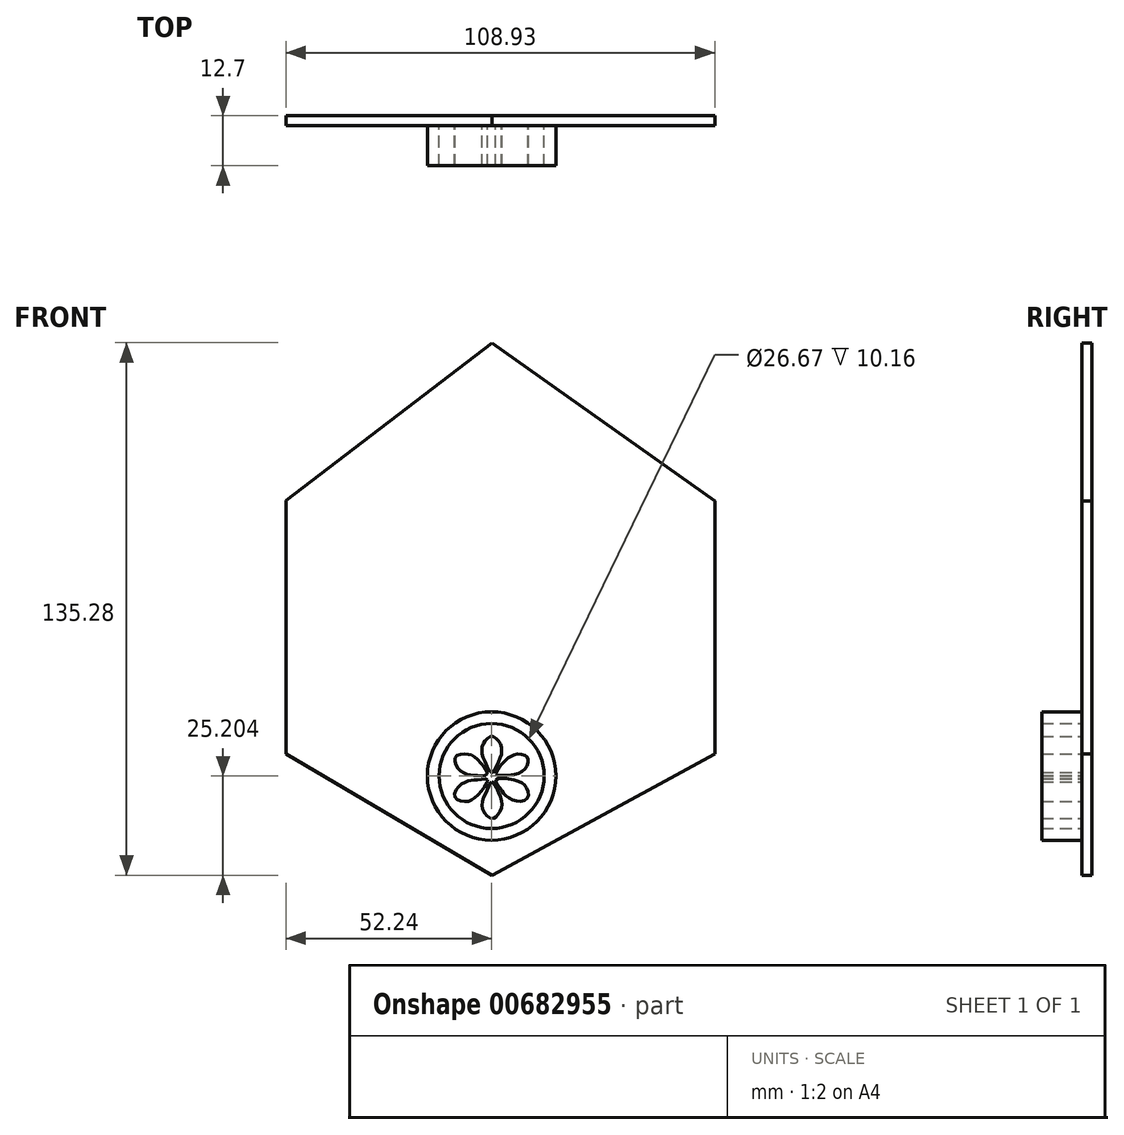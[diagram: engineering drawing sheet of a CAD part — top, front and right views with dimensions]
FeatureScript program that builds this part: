
annotation { "Feature Type Name" : "Feature", "Feature Type Description" : "" }
export const myFeature = defineFeature(function(context is Context, id is Id, definition is map)
    precondition{}
    {
        {
            var Q0;
            Q0=qCreatedBy(makeId("Front.planeOp"),FACE);
            var sketch = newSketch(context, id + "F0", { "sketchPlane" : qUnion([Q0])});
            skLineSegment(sketch, "E0", {"start": v(0, 68.56) * mm, "end": v(59.23, 26.56) * mm});
            skLineSegment(sketch, "E1", {"start": v(59.23, 26.56) * mm, "end": v(59.23, -40.56) * mm});
            skLineSegment(sketch, "E2", {"start": v(59.23, -40.56) * mm, "end": v(0, -72.79) * mm});
            skLineSegment(sketch, "E3", {"start": v(0, -72.79) * mm, "end": v(-54.78, -40.56) * mm});
            skLineSegment(sketch, "E4", {"start": v(-54.78, -40.56) * mm, "end": v(-54.78, 26.56) * mm});
            skLineSegment(sketch, "E5", {"start": v(-54.78, 26.56) * mm, "end": v(0, 68.56) * mm});
            skSolve(sketch);
        }
        {
            var Q0;
            Q0=makeQuery(id+"F0.imprint","IMPRINT",FACE,{"disambiguationData":[TD([[makeQuery(id+"F0.imprint","IMPRINT",EDGE,{"derivedFrom":sQuery(id+"F0.wireOp",EDGE,"E0")}),-1.0]])]});
            extrude(context, id + "F1", {"entities" : qUnion([Q0]), "depth" : 12.7 * mm, "offsetDistance" : 25.4 * mm});
        }
        {
            var Q0;
            Q0=makeQuery(id+"F1.opExtrude","CAP_FACE",FACE,{"disambiguationData":[OSD([sQuery(id+"F0.wireOp",EDGE,"E0"),sQuery(id+"F0.wireOp",EDGE,"E1"),sQuery(id+"F0.wireOp",EDGE,"E2"),sQuery(id+"F0.wireOp",EDGE,"E3"),sQuery(id+"F0.wireOp",EDGE,"E4"),sQuery(id+"F0.wireOp",EDGE,"E5")])],"isStart":false});
            extrude(context, id + "F2", {"entities" : qUnion([Q0]), "operationType" : NewBodyOperationType.REMOVE, "oppositeDirection" : true, "depth" : 2.54 * mm, "offsetDistance" : 25.4 * mm});
        }
        {
            var Q0;
            Q0=makeQuery(id+"F2.boolean.opBoolean","COPY",FACE,{"derivedFrom":makeQuery(id+"F2.opExtrude","CAP_FACE",FACE,{"disambiguationData":[OSD([sQuery(id+"F0.wireOp",EDGE,"E0"),sQuery(id+"F0.wireOp",EDGE,"E1"),sQuery(id+"F0.wireOp",EDGE,"E2"),sQuery(id+"F0.wireOp",EDGE,"E3"),sQuery(id+"F0.wireOp",EDGE,"E4"),sQuery(id+"F0.wireOp",EDGE,"E5")])],"isStart":false})});
            extrude(context, id + "F3", {"entities" : qUnion([Q0]), "operationType" : NewBodyOperationType.REMOVE, "oppositeDirection" : true, "depth" : 7.62 * mm, "offsetDistance" : 25.4 * mm});
        }
        {
            var Q0;
            Q0=makeQuery(id+"F1.opExtrude","SWEPT_FACE",FACE,{"disambiguationData":[OSD([sQuery(id+"F0.wireOp",EDGE,"E0")])]});
            extrude(context, id + "F4", {"entities" : qUnion([Q0]), "operationType" : NewBodyOperationType.REMOVE, "oppositeDirection" : true, "depth" : 2.54 * mm, "offsetDistance" : 25.4 * mm});
        }
        {
            var Q0;
            Q0=makeQuery(id+"F1.opExtrude","SWEPT_FACE",FACE,{"disambiguationData":[OSD([sQuery(id+"F0.wireOp",EDGE,"E5")])]});
            extrude(context, id + "F5", {"entities" : qUnion([Q0]), "operationType" : NewBodyOperationType.REMOVE, "oppositeDirection" : true, "depth" : 2.54 * mm, "offsetDistance" : 25.4 * mm});
        }
        {
            var Q0;
            Q0=makeQuery(id+"F1.opExtrude","SWEPT_FACE",FACE,{"disambiguationData":[OSD([sQuery(id+"F0.wireOp",EDGE,"E1")])]});
            extrude(context, id + "F6", {"entities" : qUnion([Q0]), "operationType" : NewBodyOperationType.REMOVE, "oppositeDirection" : true, "depth" : 2.54 * mm, "offsetDistance" : 25.4 * mm});
        }
        {
            var Q0;
            Q0=makeQuery(id+"F1.opExtrude","SWEPT_FACE",FACE,{"disambiguationData":[OSD([sQuery(id+"F0.wireOp",EDGE,"E4")])]});
            extrude(context, id + "F7", {"entities" : qUnion([Q0]), "operationType" : NewBodyOperationType.REMOVE, "oppositeDirection" : true, "depth" : 2.54 * mm, "offsetDistance" : 25.4 * mm});
        }
        {
            var Q0;
            Q0=makeQuery(id+"F1.opExtrude","SWEPT_FACE",FACE,{"disambiguationData":[OSD([sQuery(id+"F0.wireOp",EDGE,"E3")])]});
            extrude(context, id + "F8", {"entities" : qUnion([Q0]), "operationType" : NewBodyOperationType.REMOVE, "oppositeDirection" : true, "depth" : 2.54 * mm, "offsetDistance" : 25.4 * mm});
        }
        {
            var Q0;
            Q0=makeQuery(id+"F1.opExtrude","SWEPT_FACE",FACE,{"disambiguationData":[OSD([sQuery(id+"F0.wireOp",EDGE,"E2")])]});
            extrude(context, id + "F9", {"entities" : qUnion([Q0]), "operationType" : NewBodyOperationType.REMOVE, "oppositeDirection" : true, "depth" : 2.54 * mm, "offsetDistance" : 25.4 * mm});
        }
        {
            var Q0;
            Q0=makeQuery(id+"F3.boolean.opBoolean","COPY",FACE,{"derivedFrom":makeQuery(id+"F3.opExtrude","CAP_FACE",FACE,{"disambiguationData":[OSD([sQuery(id+"F0.wireOp",EDGE,"E0"),sQuery(id+"F0.wireOp",EDGE,"E1"),sQuery(id+"F0.wireOp",EDGE,"E2"),sQuery(id+"F0.wireOp",EDGE,"E3"),sQuery(id+"F0.wireOp",EDGE,"E4"),sQuery(id+"F0.wireOp",EDGE,"E5")])],"isStart":false})});
            var sketch = newSketch(context, id + "F10", { "sketchPlane" : qUnion([Q0])});
            skCircle(sketch, "E6", {"center": v(0, -44.67) * mm, "radius": 16.3 * mm});
            skCircle(sketch, "E7", {"center": v(0, -44.67) * mm, "radius": 13.34 * mm});
            skFitSpline(sketch, "E8", {"points": [v(0, -43.8) * mm, v(1.54, -41.5) * mm, v(2.48, -39.04) * mm, v(2.41, -37.1) * mm, v(1.4, -35.37) * mm, v(0, -34.56) * mm, v(-1.38, -35.4) * mm, v(-2.29, -36.83) * mm, v(-2.45, -38.87) * mm, v(-1.58, -41.34) * mm, v(0, -43.8) * mm]});
            skFitSpline(sketch, "E9", {"points": [v(1.05, -44.2) * mm, v(2.83, -41.4) * mm, v(4.62, -39.85) * mm, v(6.56, -39.1) * mm, v(8.83, -39.62) * mm, v(9.29, -40.66) * mm, v(8.57, -42.73) * mm, v(6.24, -44.22) * mm, v(3.51, -44.48) * mm, v(1.05, -44.2) * mm]});
            skFitSpline(sketch, "E10", {"points": [v(1.05, -45.62) * mm, v(5.91, -45.71) * mm, v(8.57, -47.3) * mm, v(9.19, -50.03) * mm, v(6.46, -51.06) * mm, v(3.45, -49.48) * mm, v(1.96, -47.53) * mm, v(1.05, -45.62) * mm]});
            skFitSpline(sketch, "E11", {"points": [v(0, -46.2) * mm, v(1.96, -49.15) * mm, v(2.57, -52.33) * mm, v(1.54, -54.6) * mm, v(0, -55.4) * mm, v(-2.13, -53.56) * mm, v(-2.16, -50.48) * mm, v(-0.93, -47.79) * mm, v(0, -46.2) * mm]});
            skFitSpline(sketch, "E12", {"points": [v(-1.1, -45.71) * mm, v(-3.52, -49.5) * mm, v(-6.18, -51.1) * mm, v(-9.23, -50.25) * mm, v(-8.55, -47.53) * mm, v(-5.82, -45.88) * mm, v(-3.46, -45.58) * mm, v(-1.1, -45.71) * mm]});
            skFitSpline(sketch, "E13", {"points": [v(-1.12, -44.2) * mm, v(-3.62, -40.46) * mm, v(-6.12, -39.1) * mm, v(-9.03, -39.72) * mm, v(-8.87, -42.28) * mm, v(-6.34, -44.2) * mm, v(-3.68, -44.51) * mm, v(-1.12, -44.2) * mm]});
            skSolve(sketch);
        }
        {
            var Q0;
            Q0=makeQuery(id+"F10.imprint","IMPRINT",FACE,{"disambiguationData":[TD([[makeQuery(id+"F10.imprint","IMPRINT",EDGE,{"derivedFrom":sQuery(id+"F10.wireOp",EDGE,"E8")}),1.0]])]});
            var Q1;
            Q1=makeQuery(id+"F10.imprint","IMPRINT",FACE,{"disambiguationData":[TD([[makeQuery(id+"F10.imprint","IMPRINT",EDGE,{"derivedFrom":sQuery(id+"F10.wireOp",EDGE,"E9")}),-1.0]])]});
            var Q2;
            Q2=makeQuery(id+"F10.imprint","IMPRINT",FACE,{"disambiguationData":[TD([[makeQuery(id+"F10.imprint","IMPRINT",EDGE,{"derivedFrom":sQuery(id+"F10.wireOp",EDGE,"E10")}),-1.0]])]});
            var Q3;
            Q3=makeQuery(id+"F10.imprint","IMPRINT",FACE,{"disambiguationData":[TD([[makeQuery(id+"F10.imprint","IMPRINT",EDGE,{"derivedFrom":sQuery(id+"F10.wireOp",EDGE,"E11")}),-1.0]])]});
            var Q4;
            Q4=makeQuery(id+"F10.imprint","IMPRINT",FACE,{"disambiguationData":[TD([[makeQuery(id+"F10.imprint","IMPRINT",EDGE,{"derivedFrom":sQuery(id+"F10.wireOp",EDGE,"E12")}),-1.0]])]});
            var Q5;
            Q5=makeQuery(id+"F10.imprint","IMPRINT",FACE,{"disambiguationData":[TD([[makeQuery(id+"F10.imprint","IMPRINT",EDGE,{"derivedFrom":sQuery(id+"F10.wireOp",EDGE,"E13")}),1.0]])]});
            var Q6;
            Q6=makeQuery(id+"F10.imprint","IMPRINT",FACE,{"disambiguationData":[TD([[makeQuery(id+"F10.imprint","IMPRINT",EDGE,{"derivedFrom":sQuery(id+"F10.wireOp",EDGE,"E6")}),1.0]])]});
            extrude(context, id + "F11", {"entities" : qUnion([Q0, Q1, Q2, Q3, Q4, Q5, Q6]), "operationType" : NewBodyOperationType.ADD, "depth" : 10.16 * mm, "offsetDistance" : 25.4 * mm});
        }
    });
